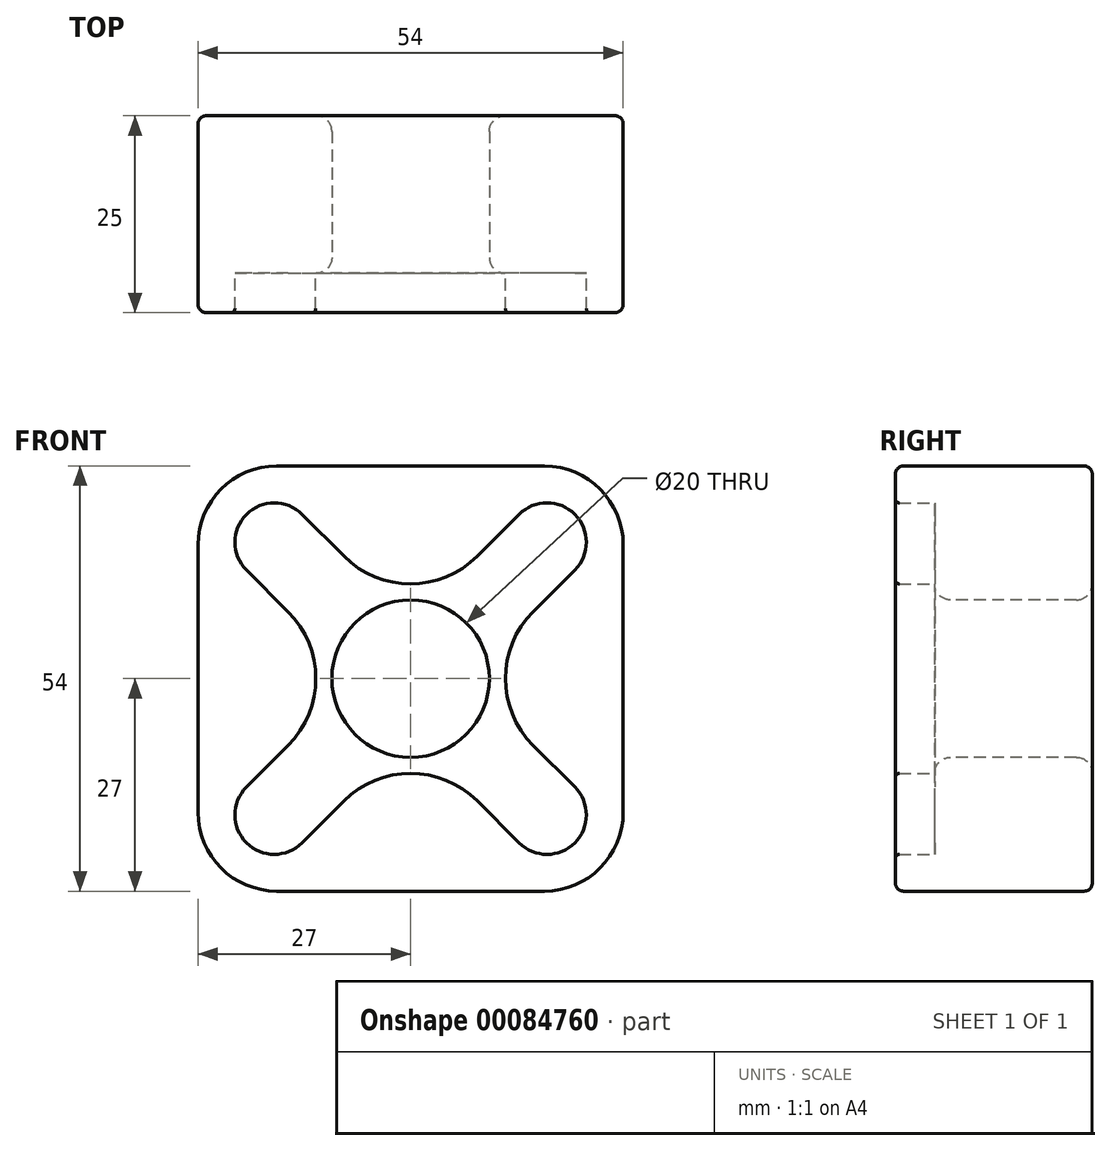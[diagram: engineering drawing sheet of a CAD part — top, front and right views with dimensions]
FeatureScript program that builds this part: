
annotation { "Feature Type Name" : "Feature", "Feature Type Description" : "" }
export const myFeature = defineFeature(function(context is Context, id is Id, definition is map)
    precondition{}
    {
        {
            var Q0;
            Q0=qCreatedBy(makeId("Front.planeOp"),FACE);
            var sketch = newSketch(context, id + "F0", { "sketchPlane" : qUnion([Q0])});
            skLineSegment(sketch, "E0", {"start": v(-17.32, -17.32) * mm, "end": v(17.32, 17.32) * mm, "construction": true});
            skLineSegment(sketch, "E1", {"start": v(-17.32, 17.32) * mm, "end": v(17.32, -17.32) * mm, "construction": true});
            skPoint(sketch, "E2", {"position": v(0, 0) * mm});
            skArc(sketch, "E3", {"start": v(-13.79, 20.86) * mm, "mid": v(-20.86, 20.86) * mm, "end": v(-20.86, 13.79) * mm});
            skArc(sketch, "E4", {"start": v(20.86, 13.79) * mm, "mid": v(20.86, 20.86) * mm, "end": v(13.79, 20.86) * mm});
            skArc(sketch, "E5", {"start": v(13.79, -20.86) * mm, "mid": v(20.86, -20.86) * mm, "end": v(20.86, -13.79) * mm});
            skArc(sketch, "E6", {"start": v(-20.86, -13.79) * mm, "mid": v(-20.86, -20.86) * mm, "end": v(-13.79, -20.86) * mm});
            skLineSegment(sketch, "E7", {"start": v(13.79, 20.86) * mm, "end": v(8.49, 15.56) * mm});
            skLineSegment(sketch, "E8", {"start": v(-13.79, 20.86) * mm, "end": v(-8.49, 15.56) * mm});
            skLineSegment(sketch, "E9", {"start": v(13.79, -20.86) * mm, "end": v(8.49, -15.56) * mm});
            skLineSegment(sketch, "E10", {"start": v(20.86, 13.79) * mm, "end": v(15.56, 8.49) * mm});
            skLineSegment(sketch, "E11.trimOffspring", {"start": v(-15.56, -8.49) * mm, "end": v(-20.86, -13.79) * mm});
            skLineSegment(sketch, "E12.trimOffspring", {"start": v(-15.56, 8.49) * mm, "end": v(-20.86, 13.79) * mm});
            skLineSegment(sketch, "E13.trimOffspring", {"start": v(-8.49, -15.56) * mm, "end": v(-13.79, -20.86) * mm});
            skLineSegment(sketch, "E14.trimOffspring", {"start": v(15.56, -8.49) * mm, "end": v(20.86, -13.79) * mm});
            skPoint(sketch, "E15", {"position": v(20.86, 20.86) * mm});
            skPoint(sketch, "E16", {"position": v(-20.86, -20.86) * mm});
            skPoint(sketch, "E17.visualSharp", {"position": v(-7.07, 0) * mm});
            skArc(sketch, "E17.filletArc", {"start": v(-15.56, -8.49) * mm, "mid": v(-12.04, 0) * mm, "end": v(-15.56, 8.49) * mm});
            skPoint(sketch, "E18.visualSharp", {"position": v(0, 7.07) * mm});
            skArc(sketch, "E18.filletArc", {"start": v(-8.49, 15.56) * mm, "mid": v(0, 12.04) * mm, "end": v(8.49, 15.56) * mm});
            skPoint(sketch, "E19.visualSharp", {"position": v(7.07, 0) * mm});
            skArc(sketch, "E19.filletArc", {"start": v(15.56, 8.49) * mm, "mid": v(12.04, 0) * mm, "end": v(15.56, -8.49) * mm});
            skPoint(sketch, "E20.visualSharp", {"position": v(0, -7.07) * mm});
            skArc(sketch, "E20.filletArc", {"start": v(8.49, -15.56) * mm, "mid": v(0, -12.04) * mm, "end": v(-8.49, -15.56) * mm});
            skLineSegment(sketch, "E21.bottom", {"start": v(27, 27) * mm, "end": v(-27, 27) * mm});
            skLineSegment(sketch, "E21.top", {"start": v(27, -27) * mm, "end": v(-27, -27) * mm});
            skLineSegment(sketch, "E21.left", {"start": v(27, 27) * mm, "end": v(27, -27) * mm});
            skLineSegment(sketch, "E21.right", {"start": v(-27, 27) * mm, "end": v(-27, -27) * mm});
            skCircle(sketch, "E22", {"center": v(0, 0) * mm, "radius": 10 * mm});
            skSolve(sketch);
        }
        {
            var Q0;
            Q0=qSketchRegion(id+"F0",true);
            extrude(context, id + "F1", {"entities" : qUnion([Q0]), "depth" : 5 * mm});
        }
        {
            var Q0;
            Q0=qSketchRegion(id+"F0",true);
            var Q1;
            Q1=makeQuery(id+"F0.imprint","IMPRINT",FACE,{"disambiguationData":[TD([[makeQuery(id+"F0.imprint","IMPRINT",EDGE,{"derivedFrom":sQuery(id+"F0.wireOp",EDGE,"E3")}),1.0]])]});
            var Q2;
            Q2=makeQuery(id+"F1.opExtrude","CAP_FACE",FACE,{"disambiguationData":[OSD([sQuery(id+"F0.wireOp",EDGE,"E3"),sQuery(id+"F0.wireOp",EDGE,"E4"),sQuery(id+"F0.wireOp",EDGE,"E5"),sQuery(id+"F0.wireOp",EDGE,"E6"),sQuery(id+"F0.wireOp",EDGE,"E7"),sQuery(id+"F0.wireOp",EDGE,"E8"),sQuery(id+"F0.wireOp",EDGE,"E9"),sQuery(id+"F0.wireOp",EDGE,"E10"),sQuery(id+"F0.wireOp",EDGE,"E11.trimOffspring"),sQuery(id+"F0.wireOp",EDGE,"E12.trimOffspring"),sQuery(id+"F0.wireOp",EDGE,"E13.trimOffspring"),sQuery(id+"F0.wireOp",EDGE,"E14.trimOffspring"),sQuery(id+"F0.wireOp",EDGE,"E17.filletArc"),sQuery(id+"F0.wireOp",EDGE,"E18.filletArc"),sQuery(id+"F0.wireOp",EDGE,"E19.filletArc"),sQuery(id+"F0.wireOp",EDGE,"E20.filletArc"),sQuery(id+"F0.wireOp",EDGE,"E21.bottom"),sQuery(id+"F0.wireOp",EDGE,"E21.top"),sQuery(id+"F0.wireOp",EDGE,"E21.left"),sQuery(id+"F0.wireOp",EDGE,"E21.right")])],"isStart":false});
            extrude(context, id + "F2", {"entities" : qUnion([Q0, Q1, Q2]), "operationType" : NewBodyOperationType.ADD, "oppositeDirection" : true, "depth" : 20 * mm});
        }
        {
            var Q0;
            Q0=makeQuery(id+"F0.imprint","IMPRINT",FACE,{"disambiguationData":[TD([[makeQuery(id+"F0.imprint","IMPRINT",EDGE,{"derivedFrom":sQuery(id+"F0.wireOp",EDGE,"E3")}),1.0]])]});
            extrude(context, id + "F3", {"entities" : qUnion([Q0]), "operationType" : NewBodyOperationType.REMOVE, "endBound" : BoundingType.THROUGH_ALL, "depth" : 25.4 * mm});
        }
        {
            var Q0;
            Q0=makeQuery(id+"F1.opExtrude","CAP_EDGE",EDGE,{"disambiguationData":[OSD([sQuery(id+"F0.wireOp",EDGE,"E14.trimOffspring")])],"isStart":false});
            fillet(context, id + "F4", {"entities" : qUnion([Q0]), "radius" : .5 * mm, "tangentPropagation" : true, "allowEdgeOverflow" : false});
        }
        {
            var Q0;
            Q0=makeQuery(id+"F2.opExtrude","SWEPT_FACE",FACE,{"disambiguationData":[OSD([sQuery(id+"F0.wireOp",EDGE,"E22")])]});
            fillet(context, id + "F5", {"entities" : qUnion([Q0]), "radius" : 2 * mm, "tangentPropagation" : true, "allowEdgeOverflow" : false});
        }
        {
            var Q0;
            {var subQ0=sQuery(id+"F0.wireOp",EDGE,"E21.left");var subQ1=sQuery(id+"F0.wireOp",EDGE,"E21.bottom");Q0=makeQuery(id+"F2.boolean.opBoolean","MERGE",EDGE,{"derivedFrom":[makeQuery(id+"F1.opExtrude","SWEPT_EDGE",EDGE,{"disambiguationData":[OSD([subQ1,subQ0])]}),makeQuery(id+"F2.opExtrude","SWEPT_EDGE",EDGE,{"disambiguationData":[OSD([subQ1,subQ0]),TDD([makeQuery(id+"F0.imprint","INTERSECT",VERTEX,{"derivedFrom":[subQ1,subQ0]})])]}),makeQuery(id+"F2.opExtrude","SWEPT_EDGE",EDGE,{"disambiguationData":[OSD([subQ1,subQ0]),TDD([makeQuery(id+"F1.opExtrude","CAP_VERTEX",VERTEX,{"disambiguationData":[OSD([subQ1,subQ0])],"isStart":false})])]})]});}
            var Q1;
            {var subQ0=sQuery(id+"F0.wireOp",EDGE,"E21.left");var subQ1=sQuery(id+"F0.wireOp",EDGE,"E21.top");Q1=makeQuery(id+"F2.boolean.opBoolean","MERGE",EDGE,{"derivedFrom":[makeQuery(id+"F1.opExtrude","SWEPT_EDGE",EDGE,{"disambiguationData":[OSD([subQ1,subQ0])]}),makeQuery(id+"F2.opExtrude","SWEPT_EDGE",EDGE,{"disambiguationData":[OSD([subQ1,subQ0]),TDD([makeQuery(id+"F0.imprint","INTERSECT",VERTEX,{"derivedFrom":[subQ1,subQ0]})])]}),makeQuery(id+"F2.opExtrude","SWEPT_EDGE",EDGE,{"disambiguationData":[OSD([subQ1,subQ0]),TDD([makeQuery(id+"F1.opExtrude","CAP_VERTEX",VERTEX,{"disambiguationData":[OSD([subQ1,subQ0])],"isStart":false})])]})]});}
            var Q2;
            {var subQ0=sQuery(id+"F0.wireOp",EDGE,"E21.right");var subQ1=sQuery(id+"F0.wireOp",EDGE,"E21.top");Q2=makeQuery(id+"F2.boolean.opBoolean","MERGE",EDGE,{"derivedFrom":[makeQuery(id+"F1.opExtrude","SWEPT_EDGE",EDGE,{"disambiguationData":[OSD([subQ1,subQ0])]}),makeQuery(id+"F2.opExtrude","SWEPT_EDGE",EDGE,{"disambiguationData":[OSD([subQ1,subQ0]),TDD([makeQuery(id+"F0.imprint","INTERSECT",VERTEX,{"derivedFrom":[subQ1,subQ0]})])]}),makeQuery(id+"F2.opExtrude","SWEPT_EDGE",EDGE,{"disambiguationData":[OSD([subQ1,subQ0]),TDD([makeQuery(id+"F1.opExtrude","CAP_VERTEX",VERTEX,{"disambiguationData":[OSD([subQ1,subQ0])],"isStart":false})])]})]});}
            var Q3;
            {var subQ0=sQuery(id+"F0.wireOp",EDGE,"E21.right");var subQ1=sQuery(id+"F0.wireOp",EDGE,"E21.bottom");Q3=makeQuery(id+"F2.boolean.opBoolean","MERGE",EDGE,{"derivedFrom":[makeQuery(id+"F1.opExtrude","SWEPT_EDGE",EDGE,{"disambiguationData":[OSD([subQ1,subQ0])]}),makeQuery(id+"F2.opExtrude","SWEPT_EDGE",EDGE,{"disambiguationData":[OSD([subQ1,subQ0]),TDD([makeQuery(id+"F0.imprint","INTERSECT",VERTEX,{"derivedFrom":[subQ1,subQ0]})])]}),makeQuery(id+"F2.opExtrude","SWEPT_EDGE",EDGE,{"disambiguationData":[OSD([subQ1,subQ0]),TDD([makeQuery(id+"F1.opExtrude","CAP_VERTEX",VERTEX,{"disambiguationData":[OSD([subQ1,subQ0])],"isStart":false})])]})]});}
            fillet(context, id + "F6", {"entities" : qUnion([Q0, Q1, Q2, Q3]), "radius" : 10 * mm, "tangentPropagation" : true, "allowEdgeOverflow" : false});
        }
        {
            var Q0;
            {var subQ0=sQuery(id+"F0.wireOp",EDGE,"E21.right");Q0=makeQuery(id+"F2.boolean.opBoolean","MERGE",FACE,{"derivedFrom":[makeQuery(id+"F1.opExtrude","SWEPT_FACE",FACE,{"disambiguationData":[OSD([subQ0])]}),makeQuery(id+"F2.opExtrude","SWEPT_FACE",FACE,{"disambiguationData":[OSD([subQ0]),TDD([makeQuery(id+"F0.imprint","IMPRINT",EDGE,{"derivedFrom":subQ0})])]}),makeQuery(id+"F2.opExtrude","SWEPT_FACE",FACE,{"disambiguationData":[OSD([subQ0]),TDD([makeQuery(id+"F1.opExtrude","CAP_EDGE",EDGE,{"disambiguationData":[OSD([subQ0])],"isStart":false})])]})]});}
            fillet(context, id + "F7", {"entities" : qUnion([Q0]), "radius" : 1 * mm, "tangentPropagation" : true, "allowEdgeOverflow" : false});
        }
    });
